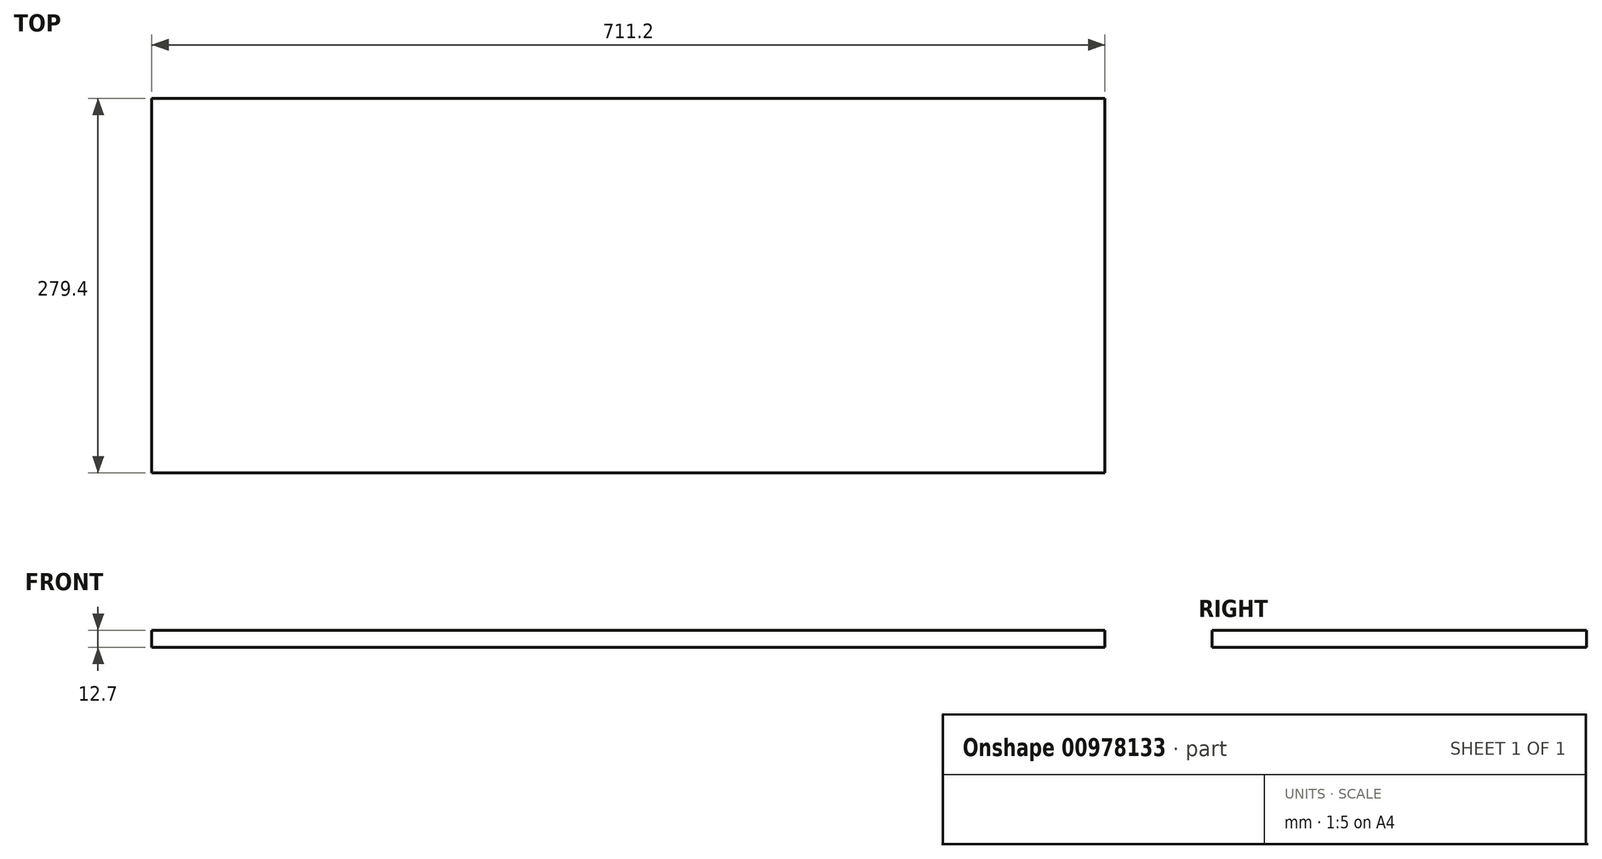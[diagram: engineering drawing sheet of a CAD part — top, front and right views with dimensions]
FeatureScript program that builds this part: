
annotation { "Feature Type Name" : "Feature", "Feature Type Description" : "" }
export const myFeature = defineFeature(function(context is Context, id is Id, definition is map)
    precondition{}
    {
        {
            var Q0;
            Q0=qCreatedBy(makeId("Top.planeOp"),FACE);
            var sketch = newSketch(context, id + "F0", { "sketchPlane" : qUnion([Q0])});
            skLineSegment(sketch, "E0.bottom", {"start": v(0, 0) * mm, "end": v(711.2, 0) * mm});
            skLineSegment(sketch, "E0.top", {"start": v(0, 279.4) * mm, "end": v(711.2, 279.4) * mm});
            skLineSegment(sketch, "E0.left", {"start": v(0, 0) * mm, "end": v(0, 279.4) * mm});
            skLineSegment(sketch, "E0.right", {"start": v(711.2, 0) * mm, "end": v(711.2, 279.4) * mm});
            skSolve(sketch);
        }
        {
            var Q0;
            Q0=makeQuery(id+"F0.imprint","IMPRINT",FACE,{"disambiguationData":[TD([[makeQuery(id+"F0.imprint","IMPRINT",EDGE,{"derivedFrom":sQuery(id+"F0.wireOp",EDGE,"E0.bottom")}),1.0]])]});
            extrude(context, id + "F1", {"entities" : qUnion([Q0]), "depth" : 12.7 * mm, "offsetDistance" : 25.4 * mm});
        }
    });
